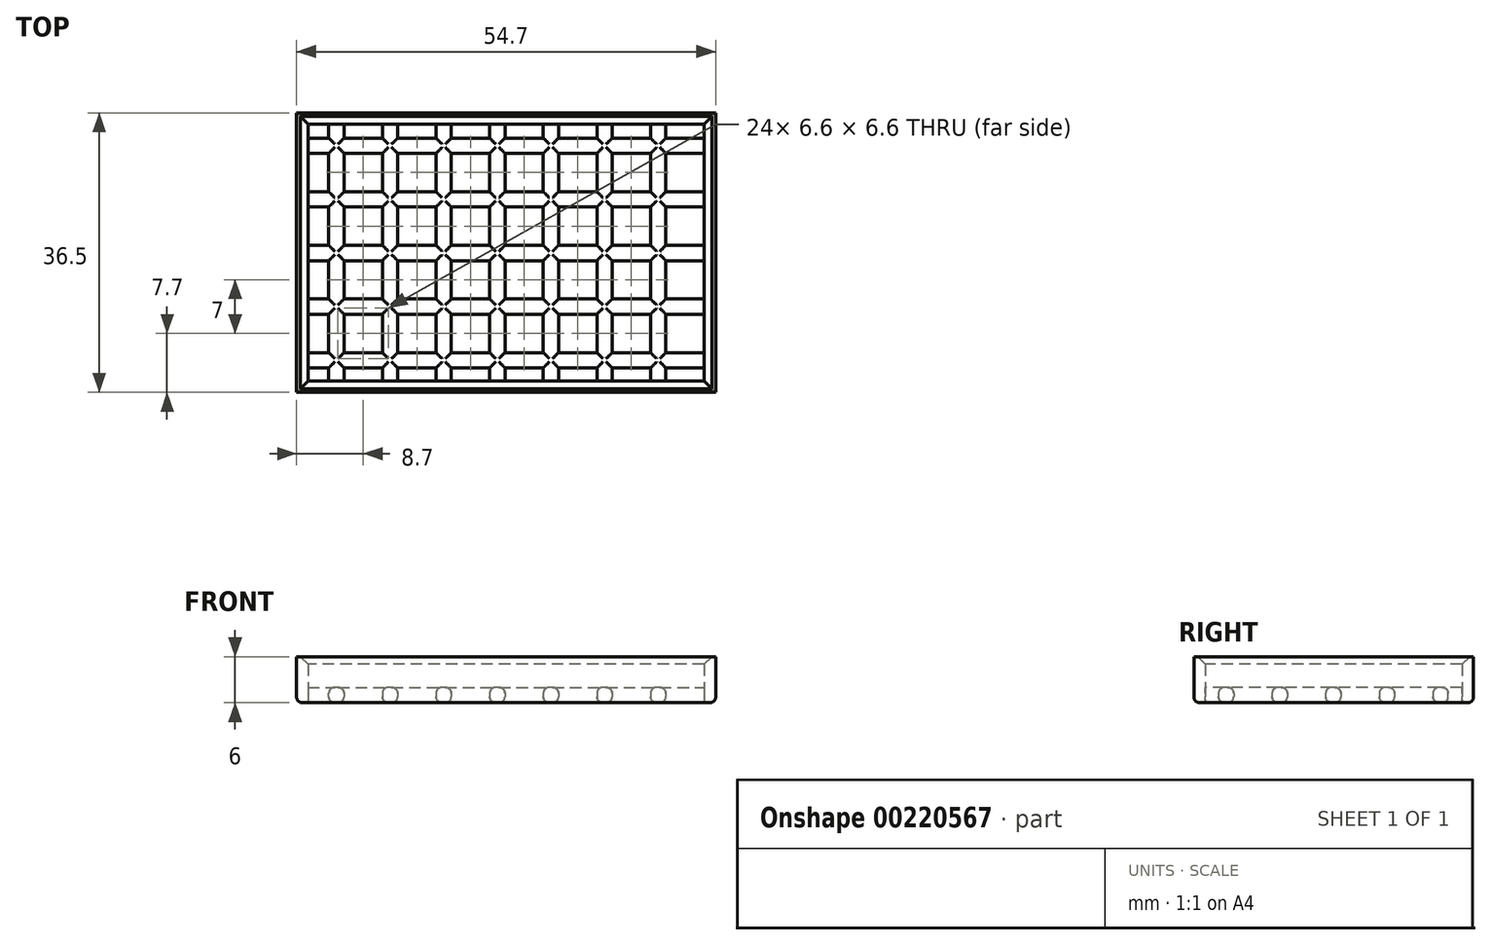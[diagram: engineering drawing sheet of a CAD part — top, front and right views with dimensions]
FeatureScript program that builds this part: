
annotation { "Feature Type Name" : "Feature", "Feature Type Description" : "" }
export const myFeature = defineFeature(function(context is Context, id is Id, definition is map)
    precondition{}
    {
        {
            var Q0;
            Q0=qCreatedBy(makeId("Top.planeOp"),FACE);
            var sketch = newSketch(context, id + "F0", { "sketchPlane" : qUnion([Q0])});
            skLineSegment(sketch, "E0.bottom", {"start": v(0, 36.5) * mm, "end": v(54.7, 36.5) * mm});
            skLineSegment(sketch, "E0.top", {"start": v(0, 0) * mm, "end": v(54.7, 0) * mm});
            skLineSegment(sketch, "E0.left", {"start": v(0, 36.5) * mm, "end": v(0, 0) * mm});
            skLineSegment(sketch, "E0.right", {"start": v(54.7, 36.5) * mm, "end": v(54.7, 0) * mm});
            skSolve(sketch);
        }
        {
            var Q0;
            Q0 = qSketchRegion(id + "F0", true);
            extrude(context, id + "F1", {"entities" : qUnion([Q0]), "oppositeDirection" : true, "depth" : 2 * mm});
        }
        {
            var Q0;
            Q0=makeQuery(id+"F1.opExtrude","CAP_FACE",FACE,{"disambiguationData":[OSD([sQuery(id+"F0.wireOp",EDGE,"E0.bottom"),sQuery(id+"F0.wireOp",EDGE,"E0.top"),sQuery(id+"F0.wireOp",EDGE,"E0.left"),sQuery(id+"F0.wireOp",EDGE,"E0.right")])],"isStart":true});
            var sketch = newSketch(context, id + "F2", { "sketchPlane" : qUnion([Q0])});
            skLineSegment(sketch, "E1.bottom", {"start": v(-0.8, 38.2) * mm, "end": v(4.2, 38.2) * mm});
            skLineSegment(sketch, "E1.top", {"start": v(-0.8, 33.2) * mm, "end": v(4.2, 33.2) * mm});
            skLineSegment(sketch, "E1.left", {"start": v(-0.8, 38.2) * mm, "end": v(-0.8, 33.2) * mm});
            skLineSegment(sketch, "E1.right", {"start": v(4.2, 38.2) * mm, "end": v(4.2, 33.2) * mm});
            skLineSegment(sketch, "E2.0.1.0", {"start": v(-0.8, 31.2) * mm, "end": v(4.2, 31.2) * mm});
            skLineSegment(sketch, "E2.0.1.1", {"start": v(-0.8, 26.2) * mm, "end": v(4.2, 26.2) * mm});
            skLineSegment(sketch, "E2.0.1.2", {"start": v(-0.8, 31.2) * mm, "end": v(-0.8, 26.2) * mm});
            skLineSegment(sketch, "E2.0.1.3", {"start": v(4.2, 31.2) * mm, "end": v(4.2, 26.2) * mm});
            skLineSegment(sketch, "E2.0.2.0", {"start": v(-0.8, 24.2) * mm, "end": v(4.2, 24.2) * mm});
            skLineSegment(sketch, "E2.0.2.1", {"start": v(-0.8, 19.2) * mm, "end": v(4.2, 19.2) * mm});
            skLineSegment(sketch, "E2.0.2.2", {"start": v(-0.8, 24.2) * mm, "end": v(-0.8, 19.2) * mm});
            skLineSegment(sketch, "E2.0.2.3", {"start": v(4.2, 24.2) * mm, "end": v(4.2, 19.2) * mm});
            skLineSegment(sketch, "E2.0.3.0", {"start": v(-0.8, 17.2) * mm, "end": v(4.2, 17.2) * mm});
            skLineSegment(sketch, "E2.0.3.1", {"start": v(-0.8, 12.2) * mm, "end": v(4.2, 12.2) * mm});
            skLineSegment(sketch, "E2.0.3.2", {"start": v(-0.8, 17.2) * mm, "end": v(-0.8, 12.2) * mm});
            skLineSegment(sketch, "E2.0.3.3", {"start": v(4.2, 17.2) * mm, "end": v(4.2, 12.2) * mm});
            skLineSegment(sketch, "E2.0.4.0", {"start": v(-0.8, 10.2) * mm, "end": v(4.2, 10.2) * mm});
            skLineSegment(sketch, "E2.0.4.1", {"start": v(-0.8, 5.2) * mm, "end": v(4.2, 5.2) * mm});
            skLineSegment(sketch, "E2.0.4.2", {"start": v(-0.8, 10.2) * mm, "end": v(-0.8, 5.2) * mm});
            skLineSegment(sketch, "E2.0.4.3", {"start": v(4.2, 10.2) * mm, "end": v(4.2, 5.2) * mm});
            skLineSegment(sketch, "E2.0.5.0", {"start": v(-0.8, 3.2) * mm, "end": v(4.2, 3.2) * mm});
            skLineSegment(sketch, "E2.0.5.1", {"start": v(-0.8, -1.8) * mm, "end": v(4.2, -1.8) * mm});
            skLineSegment(sketch, "E2.0.5.2", {"start": v(-0.8, 3.2) * mm, "end": v(-0.8, -1.8) * mm});
            skLineSegment(sketch, "E2.0.5.3", {"start": v(4.2, 3.2) * mm, "end": v(4.2, -1.8) * mm});
            skLineSegment(sketch, "E2.1.0.0", {"start": v(6.2, 38.2) * mm, "end": v(11.2, 38.2) * mm});
            skLineSegment(sketch, "E2.1.0.1", {"start": v(6.2, 33.2) * mm, "end": v(11.2, 33.2) * mm});
            skLineSegment(sketch, "E2.1.0.2", {"start": v(6.2, 38.2) * mm, "end": v(6.2, 33.2) * mm});
            skLineSegment(sketch, "E2.1.0.3", {"start": v(11.2, 38.2) * mm, "end": v(11.2, 33.2) * mm});
            skLineSegment(sketch, "E2.1.1.0", {"start": v(6.2, 31.2) * mm, "end": v(11.2, 31.2) * mm});
            skLineSegment(sketch, "E2.1.1.1", {"start": v(6.2, 26.2) * mm, "end": v(11.2, 26.2) * mm});
            skLineSegment(sketch, "E2.1.1.2", {"start": v(6.2, 31.2) * mm, "end": v(6.2, 26.2) * mm});
            skLineSegment(sketch, "E2.1.1.3", {"start": v(11.2, 31.2) * mm, "end": v(11.2, 26.2) * mm});
            skLineSegment(sketch, "E2.1.2.0", {"start": v(6.2, 24.2) * mm, "end": v(11.2, 24.2) * mm});
            skLineSegment(sketch, "E2.1.2.1", {"start": v(6.2, 19.2) * mm, "end": v(11.2, 19.2) * mm});
            skLineSegment(sketch, "E2.1.2.2", {"start": v(6.2, 24.2) * mm, "end": v(6.2, 19.2) * mm});
            skLineSegment(sketch, "E2.1.2.3", {"start": v(11.2, 24.2) * mm, "end": v(11.2, 19.2) * mm});
            skLineSegment(sketch, "E2.1.3.0", {"start": v(6.2, 17.2) * mm, "end": v(11.2, 17.2) * mm});
            skLineSegment(sketch, "E2.1.3.1", {"start": v(6.2, 12.2) * mm, "end": v(11.2, 12.2) * mm});
            skLineSegment(sketch, "E2.1.3.2", {"start": v(6.2, 17.2) * mm, "end": v(6.2, 12.2) * mm});
            skLineSegment(sketch, "E2.1.3.3", {"start": v(11.2, 17.2) * mm, "end": v(11.2, 12.2) * mm});
            skLineSegment(sketch, "E2.1.4.0", {"start": v(6.2, 10.2) * mm, "end": v(11.2, 10.2) * mm});
            skLineSegment(sketch, "E2.1.4.1", {"start": v(6.2, 5.2) * mm, "end": v(11.2, 5.2) * mm});
            skLineSegment(sketch, "E2.1.4.2", {"start": v(6.2, 10.2) * mm, "end": v(6.2, 5.2) * mm});
            skLineSegment(sketch, "E2.1.4.3", {"start": v(11.2, 10.2) * mm, "end": v(11.2, 5.2) * mm});
            skLineSegment(sketch, "E2.1.5.0", {"start": v(6.2, 3.2) * mm, "end": v(11.2, 3.2) * mm});
            skLineSegment(sketch, "E2.1.5.1", {"start": v(6.2, -1.8) * mm, "end": v(11.2, -1.8) * mm});
            skLineSegment(sketch, "E2.1.5.2", {"start": v(6.2, 3.2) * mm, "end": v(6.2, -1.8) * mm});
            skLineSegment(sketch, "E2.1.5.3", {"start": v(11.2, 3.2) * mm, "end": v(11.2, -1.8) * mm});
            skLineSegment(sketch, "E2.2.0.0", {"start": v(13.2, 38.2) * mm, "end": v(18.2, 38.2) * mm});
            skLineSegment(sketch, "E2.2.0.1", {"start": v(13.2, 33.2) * mm, "end": v(18.2, 33.2) * mm});
            skLineSegment(sketch, "E2.2.0.2", {"start": v(13.2, 38.2) * mm, "end": v(13.2, 33.2) * mm});
            skLineSegment(sketch, "E2.2.0.3", {"start": v(18.2, 38.2) * mm, "end": v(18.2, 33.2) * mm});
            skLineSegment(sketch, "E2.2.1.0", {"start": v(13.2, 31.2) * mm, "end": v(18.2, 31.2) * mm});
            skLineSegment(sketch, "E2.2.1.1", {"start": v(13.2, 26.2) * mm, "end": v(18.2, 26.2) * mm});
            skLineSegment(sketch, "E2.2.1.2", {"start": v(13.2, 31.2) * mm, "end": v(13.2, 26.2) * mm});
            skLineSegment(sketch, "E2.2.1.3", {"start": v(18.2, 31.2) * mm, "end": v(18.2, 26.2) * mm});
            skLineSegment(sketch, "E2.2.2.0", {"start": v(13.2, 24.2) * mm, "end": v(18.2, 24.2) * mm});
            skLineSegment(sketch, "E2.2.2.1", {"start": v(13.2, 19.2) * mm, "end": v(18.2, 19.2) * mm});
            skLineSegment(sketch, "E2.2.2.2", {"start": v(13.2, 24.2) * mm, "end": v(13.2, 19.2) * mm});
            skLineSegment(sketch, "E2.2.2.3", {"start": v(18.2, 24.2) * mm, "end": v(18.2, 19.2) * mm});
            skLineSegment(sketch, "E2.2.3.0", {"start": v(13.2, 17.2) * mm, "end": v(18.2, 17.2) * mm});
            skLineSegment(sketch, "E2.2.3.1", {"start": v(13.2, 12.2) * mm, "end": v(18.2, 12.2) * mm});
            skLineSegment(sketch, "E2.2.3.2", {"start": v(13.2, 17.2) * mm, "end": v(13.2, 12.2) * mm});
            skLineSegment(sketch, "E2.2.3.3", {"start": v(18.2, 17.2) * mm, "end": v(18.2, 12.2) * mm});
            skLineSegment(sketch, "E2.2.4.0", {"start": v(13.2, 10.2) * mm, "end": v(18.2, 10.2) * mm});
            skLineSegment(sketch, "E2.2.4.1", {"start": v(13.2, 5.2) * mm, "end": v(18.2, 5.2) * mm});
            skLineSegment(sketch, "E2.2.4.2", {"start": v(13.2, 10.2) * mm, "end": v(13.2, 5.2) * mm});
            skLineSegment(sketch, "E2.2.4.3", {"start": v(18.2, 10.2) * mm, "end": v(18.2, 5.2) * mm});
            skLineSegment(sketch, "E2.2.5.0", {"start": v(13.2, 3.2) * mm, "end": v(18.2, 3.2) * mm});
            skLineSegment(sketch, "E2.2.5.1", {"start": v(13.2, -1.8) * mm, "end": v(18.2, -1.8) * mm});
            skLineSegment(sketch, "E2.2.5.2", {"start": v(13.2, 3.2) * mm, "end": v(13.2, -1.8) * mm});
            skLineSegment(sketch, "E2.2.5.3", {"start": v(18.2, 3.2) * mm, "end": v(18.2, -1.8) * mm});
            skLineSegment(sketch, "E2.3.0.0", {"start": v(20.2, 38.2) * mm, "end": v(25.2, 38.2) * mm});
            skLineSegment(sketch, "E2.3.0.1", {"start": v(20.2, 33.2) * mm, "end": v(25.2, 33.2) * mm});
            skLineSegment(sketch, "E2.3.0.2", {"start": v(20.2, 38.2) * mm, "end": v(20.2, 33.2) * mm});
            skLineSegment(sketch, "E2.3.0.3", {"start": v(25.2, 38.2) * mm, "end": v(25.2, 33.2) * mm});
            skLineSegment(sketch, "E2.3.1.0", {"start": v(20.2, 31.2) * mm, "end": v(25.2, 31.2) * mm});
            skLineSegment(sketch, "E2.3.1.1", {"start": v(20.2, 26.2) * mm, "end": v(25.2, 26.2) * mm});
            skLineSegment(sketch, "E2.3.1.2", {"start": v(20.2, 31.2) * mm, "end": v(20.2, 26.2) * mm});
            skLineSegment(sketch, "E2.3.1.3", {"start": v(25.2, 31.2) * mm, "end": v(25.2, 26.2) * mm});
            skLineSegment(sketch, "E2.3.2.0", {"start": v(20.2, 24.2) * mm, "end": v(25.2, 24.2) * mm});
            skLineSegment(sketch, "E2.3.2.1", {"start": v(20.2, 19.2) * mm, "end": v(25.2, 19.2) * mm});
            skLineSegment(sketch, "E2.3.2.2", {"start": v(20.2, 24.2) * mm, "end": v(20.2, 19.2) * mm});
            skLineSegment(sketch, "E2.3.2.3", {"start": v(25.2, 24.2) * mm, "end": v(25.2, 19.2) * mm});
            skLineSegment(sketch, "E2.3.3.0", {"start": v(20.2, 17.2) * mm, "end": v(25.2, 17.2) * mm});
            skLineSegment(sketch, "E2.3.3.1", {"start": v(20.2, 12.2) * mm, "end": v(25.2, 12.2) * mm});
            skLineSegment(sketch, "E2.3.3.2", {"start": v(20.2, 17.2) * mm, "end": v(20.2, 12.2) * mm});
            skLineSegment(sketch, "E2.3.3.3", {"start": v(25.2, 17.2) * mm, "end": v(25.2, 12.2) * mm});
            skLineSegment(sketch, "E2.3.4.0", {"start": v(20.2, 10.2) * mm, "end": v(25.2, 10.2) * mm});
            skLineSegment(sketch, "E2.3.4.1", {"start": v(20.2, 5.2) * mm, "end": v(25.2, 5.2) * mm});
            skLineSegment(sketch, "E2.3.4.2", {"start": v(20.2, 10.2) * mm, "end": v(20.2, 5.2) * mm});
            skLineSegment(sketch, "E2.3.4.3", {"start": v(25.2, 10.2) * mm, "end": v(25.2, 5.2) * mm});
            skLineSegment(sketch, "E2.3.5.0", {"start": v(20.2, 3.2) * mm, "end": v(25.2, 3.2) * mm});
            skLineSegment(sketch, "E2.3.5.1", {"start": v(20.2, -1.8) * mm, "end": v(25.2, -1.8) * mm});
            skLineSegment(sketch, "E2.3.5.2", {"start": v(20.2, 3.2) * mm, "end": v(20.2, -1.8) * mm});
            skLineSegment(sketch, "E2.3.5.3", {"start": v(25.2, 3.2) * mm, "end": v(25.2, -1.8) * mm});
            skLineSegment(sketch, "E2.4.0.0", {"start": v(27.2, 38.2) * mm, "end": v(32.2, 38.2) * mm});
            skLineSegment(sketch, "E2.4.0.1", {"start": v(27.2, 33.2) * mm, "end": v(32.2, 33.2) * mm});
            skLineSegment(sketch, "E2.4.0.2", {"start": v(27.2, 38.2) * mm, "end": v(27.2, 33.2) * mm});
            skLineSegment(sketch, "E2.4.0.3", {"start": v(32.2, 38.2) * mm, "end": v(32.2, 33.2) * mm});
            skLineSegment(sketch, "E2.4.1.0", {"start": v(27.2, 31.2) * mm, "end": v(32.2, 31.2) * mm});
            skLineSegment(sketch, "E2.4.1.1", {"start": v(27.2, 26.2) * mm, "end": v(32.2, 26.2) * mm});
            skLineSegment(sketch, "E2.4.1.2", {"start": v(27.2, 31.2) * mm, "end": v(27.2, 26.2) * mm});
            skLineSegment(sketch, "E2.4.1.3", {"start": v(32.2, 31.2) * mm, "end": v(32.2, 26.2) * mm});
            skLineSegment(sketch, "E2.4.2.0", {"start": v(27.2, 24.2) * mm, "end": v(32.2, 24.2) * mm});
            skLineSegment(sketch, "E2.4.2.1", {"start": v(27.2, 19.2) * mm, "end": v(32.2, 19.2) * mm});
            skLineSegment(sketch, "E2.4.2.2", {"start": v(27.2, 24.2) * mm, "end": v(27.2, 19.2) * mm});
            skLineSegment(sketch, "E2.4.2.3", {"start": v(32.2, 24.2) * mm, "end": v(32.2, 19.2) * mm});
            skLineSegment(sketch, "E2.4.3.0", {"start": v(27.2, 17.2) * mm, "end": v(32.2, 17.2) * mm});
            skLineSegment(sketch, "E2.4.3.1", {"start": v(27.2, 12.2) * mm, "end": v(32.2, 12.2) * mm});
            skLineSegment(sketch, "E2.4.3.2", {"start": v(27.2, 17.2) * mm, "end": v(27.2, 12.2) * mm});
            skLineSegment(sketch, "E2.4.3.3", {"start": v(32.2, 17.2) * mm, "end": v(32.2, 12.2) * mm});
            skLineSegment(sketch, "E2.4.4.0", {"start": v(27.2, 10.2) * mm, "end": v(32.2, 10.2) * mm});
            skLineSegment(sketch, "E2.4.4.1", {"start": v(27.2, 5.2) * mm, "end": v(32.2, 5.2) * mm});
            skLineSegment(sketch, "E2.4.4.2", {"start": v(27.2, 10.2) * mm, "end": v(27.2, 5.2) * mm});
            skLineSegment(sketch, "E2.4.4.3", {"start": v(32.2, 10.2) * mm, "end": v(32.2, 5.2) * mm});
            skLineSegment(sketch, "E2.4.5.0", {"start": v(27.2, 3.2) * mm, "end": v(32.2, 3.2) * mm});
            skLineSegment(sketch, "E2.4.5.1", {"start": v(27.2, -1.8) * mm, "end": v(32.2, -1.8) * mm});
            skLineSegment(sketch, "E2.4.5.2", {"start": v(27.2, 3.2) * mm, "end": v(27.2, -1.8) * mm});
            skLineSegment(sketch, "E2.4.5.3", {"start": v(32.2, 3.2) * mm, "end": v(32.2, -1.8) * mm});
            skLineSegment(sketch, "E2.5.0.0", {"start": v(34.2, 38.2) * mm, "end": v(39.2, 38.2) * mm});
            skLineSegment(sketch, "E2.5.0.1", {"start": v(34.2, 33.2) * mm, "end": v(39.2, 33.2) * mm});
            skLineSegment(sketch, "E2.5.0.2", {"start": v(34.2, 38.2) * mm, "end": v(34.2, 33.2) * mm});
            skLineSegment(sketch, "E2.5.0.3", {"start": v(39.2, 38.2) * mm, "end": v(39.2, 33.2) * mm});
            skLineSegment(sketch, "E2.5.1.0", {"start": v(34.2, 31.2) * mm, "end": v(39.2, 31.2) * mm});
            skLineSegment(sketch, "E2.5.1.1", {"start": v(34.2, 26.2) * mm, "end": v(39.2, 26.2) * mm});
            skLineSegment(sketch, "E2.5.1.2", {"start": v(34.2, 31.2) * mm, "end": v(34.2, 26.2) * mm});
            skLineSegment(sketch, "E2.5.1.3", {"start": v(39.2, 31.2) * mm, "end": v(39.2, 26.2) * mm});
            skLineSegment(sketch, "E2.5.2.0", {"start": v(34.2, 24.2) * mm, "end": v(39.2, 24.2) * mm});
            skLineSegment(sketch, "E2.5.2.1", {"start": v(34.2, 19.2) * mm, "end": v(39.2, 19.2) * mm});
            skLineSegment(sketch, "E2.5.2.2", {"start": v(34.2, 24.2) * mm, "end": v(34.2, 19.2) * mm});
            skLineSegment(sketch, "E2.5.2.3", {"start": v(39.2, 24.2) * mm, "end": v(39.2, 19.2) * mm});
            skLineSegment(sketch, "E2.5.3.0", {"start": v(34.2, 17.2) * mm, "end": v(39.2, 17.2) * mm});
            skLineSegment(sketch, "E2.5.3.1", {"start": v(34.2, 12.2) * mm, "end": v(39.2, 12.2) * mm});
            skLineSegment(sketch, "E2.5.3.2", {"start": v(34.2, 17.2) * mm, "end": v(34.2, 12.2) * mm});
            skLineSegment(sketch, "E2.5.3.3", {"start": v(39.2, 17.2) * mm, "end": v(39.2, 12.2) * mm});
            skLineSegment(sketch, "E2.5.4.0", {"start": v(34.2, 10.2) * mm, "end": v(39.2, 10.2) * mm});
            skLineSegment(sketch, "E2.5.4.1", {"start": v(34.2, 5.2) * mm, "end": v(39.2, 5.2) * mm});
            skLineSegment(sketch, "E2.5.4.2", {"start": v(34.2, 10.2) * mm, "end": v(34.2, 5.2) * mm});
            skLineSegment(sketch, "E2.5.4.3", {"start": v(39.2, 10.2) * mm, "end": v(39.2, 5.2) * mm});
            skLineSegment(sketch, "E2.5.5.0", {"start": v(34.2, 3.2) * mm, "end": v(39.2, 3.2) * mm});
            skLineSegment(sketch, "E2.5.5.1", {"start": v(34.2, -1.8) * mm, "end": v(39.2, -1.8) * mm});
            skLineSegment(sketch, "E2.5.5.2", {"start": v(34.2, 3.2) * mm, "end": v(34.2, -1.8) * mm});
            skLineSegment(sketch, "E2.5.5.3", {"start": v(39.2, 3.2) * mm, "end": v(39.2, -1.8) * mm});
            skLineSegment(sketch, "E2.6.0.0", {"start": v(41.2, 38.2) * mm, "end": v(46.2, 38.2) * mm});
            skLineSegment(sketch, "E2.6.0.1", {"start": v(41.2, 33.2) * mm, "end": v(46.2, 33.2) * mm});
            skLineSegment(sketch, "E2.6.0.2", {"start": v(41.2, 38.2) * mm, "end": v(41.2, 33.2) * mm});
            skLineSegment(sketch, "E2.6.0.3", {"start": v(46.2, 38.2) * mm, "end": v(46.2, 33.2) * mm});
            skLineSegment(sketch, "E2.6.1.0", {"start": v(41.2, 31.2) * mm, "end": v(46.2, 31.2) * mm});
            skLineSegment(sketch, "E2.6.1.1", {"start": v(41.2, 26.2) * mm, "end": v(46.2, 26.2) * mm});
            skLineSegment(sketch, "E2.6.1.2", {"start": v(41.2, 31.2) * mm, "end": v(41.2, 26.2) * mm});
            skLineSegment(sketch, "E2.6.1.3", {"start": v(46.2, 31.2) * mm, "end": v(46.2, 26.2) * mm});
            skLineSegment(sketch, "E2.6.2.0", {"start": v(41.2, 24.2) * mm, "end": v(46.2, 24.2) * mm});
            skLineSegment(sketch, "E2.6.2.1", {"start": v(41.2, 19.2) * mm, "end": v(46.2, 19.2) * mm});
            skLineSegment(sketch, "E2.6.2.2", {"start": v(41.2, 24.2) * mm, "end": v(41.2, 19.2) * mm});
            skLineSegment(sketch, "E2.6.2.3", {"start": v(46.2, 24.2) * mm, "end": v(46.2, 19.2) * mm});
            skLineSegment(sketch, "E2.6.3.0", {"start": v(41.2, 17.2) * mm, "end": v(46.2, 17.2) * mm});
            skLineSegment(sketch, "E2.6.3.1", {"start": v(41.2, 12.2) * mm, "end": v(46.2, 12.2) * mm});
            skLineSegment(sketch, "E2.6.3.2", {"start": v(41.2, 17.2) * mm, "end": v(41.2, 12.2) * mm});
            skLineSegment(sketch, "E2.6.3.3", {"start": v(46.2, 17.2) * mm, "end": v(46.2, 12.2) * mm});
            skLineSegment(sketch, "E2.6.4.0", {"start": v(41.2, 10.2) * mm, "end": v(46.2, 10.2) * mm});
            skLineSegment(sketch, "E2.6.4.1", {"start": v(41.2, 5.2) * mm, "end": v(46.2, 5.2) * mm});
            skLineSegment(sketch, "E2.6.4.2", {"start": v(41.2, 10.2) * mm, "end": v(41.2, 5.2) * mm});
            skLineSegment(sketch, "E2.6.4.3", {"start": v(46.2, 10.2) * mm, "end": v(46.2, 5.2) * mm});
            skLineSegment(sketch, "E2.6.5.0", {"start": v(41.2, 3.2) * mm, "end": v(46.2, 3.2) * mm});
            skLineSegment(sketch, "E2.6.5.1", {"start": v(41.2, -1.8) * mm, "end": v(46.2, -1.8) * mm});
            skLineSegment(sketch, "E2.6.5.2", {"start": v(41.2, 3.2) * mm, "end": v(41.2, -1.8) * mm});
            skLineSegment(sketch, "E2.6.5.3", {"start": v(46.2, 3.2) * mm, "end": v(46.2, -1.8) * mm});
            skLineSegment(sketch, "E2.7.0.0", {"start": v(48.2, 38.2) * mm, "end": v(53.2, 38.2) * mm});
            skLineSegment(sketch, "E2.7.0.1", {"start": v(48.2, 33.2) * mm, "end": v(53.2, 33.2) * mm});
            skLineSegment(sketch, "E2.7.0.2", {"start": v(48.2, 38.2) * mm, "end": v(48.2, 33.2) * mm});
            skLineSegment(sketch, "E2.7.0.3", {"start": v(53.2, 38.2) * mm, "end": v(53.2, 33.2) * mm});
            skLineSegment(sketch, "E2.7.1.0", {"start": v(48.2, 31.2) * mm, "end": v(53.2, 31.2) * mm});
            skLineSegment(sketch, "E2.7.1.1", {"start": v(48.2, 26.2) * mm, "end": v(53.2, 26.2) * mm});
            skLineSegment(sketch, "E2.7.1.2", {"start": v(48.2, 31.2) * mm, "end": v(48.2, 26.2) * mm});
            skLineSegment(sketch, "E2.7.1.3", {"start": v(53.2, 31.2) * mm, "end": v(53.2, 26.2) * mm});
            skLineSegment(sketch, "E2.7.2.0", {"start": v(48.2, 24.2) * mm, "end": v(53.2, 24.2) * mm});
            skLineSegment(sketch, "E2.7.2.1", {"start": v(48.2, 19.2) * mm, "end": v(53.2, 19.2) * mm});
            skLineSegment(sketch, "E2.7.2.2", {"start": v(48.2, 24.2) * mm, "end": v(48.2, 19.2) * mm});
            skLineSegment(sketch, "E2.7.2.3", {"start": v(53.2, 24.2) * mm, "end": v(53.2, 19.2) * mm});
            skLineSegment(sketch, "E2.7.3.0", {"start": v(48.2, 17.2) * mm, "end": v(53.2, 17.2) * mm});
            skLineSegment(sketch, "E2.7.3.1", {"start": v(48.2, 12.2) * mm, "end": v(53.2, 12.2) * mm});
            skLineSegment(sketch, "E2.7.3.2", {"start": v(48.2, 17.2) * mm, "end": v(48.2, 12.2) * mm});
            skLineSegment(sketch, "E2.7.3.3", {"start": v(53.2, 17.2) * mm, "end": v(53.2, 12.2) * mm});
            skLineSegment(sketch, "E2.7.4.0", {"start": v(48.2, 10.2) * mm, "end": v(53.2, 10.2) * mm});
            skLineSegment(sketch, "E2.7.4.1", {"start": v(48.2, 5.2) * mm, "end": v(53.2, 5.2) * mm});
            skLineSegment(sketch, "E2.7.4.2", {"start": v(48.2, 10.2) * mm, "end": v(48.2, 5.2) * mm});
            skLineSegment(sketch, "E2.7.4.3", {"start": v(53.2, 10.2) * mm, "end": v(53.2, 5.2) * mm});
            skLineSegment(sketch, "E2.7.5.0", {"start": v(48.2, 3.2) * mm, "end": v(53.2, 3.2) * mm});
            skLineSegment(sketch, "E2.7.5.1", {"start": v(48.2, -1.8) * mm, "end": v(53.2, -1.8) * mm});
            skLineSegment(sketch, "E2.7.5.2", {"start": v(48.2, 3.2) * mm, "end": v(48.2, -1.8) * mm});
            skLineSegment(sketch, "E2.7.5.3", {"start": v(53.2, 3.2) * mm, "end": v(53.2, -1.8) * mm});
            skLineSegment(sketch, "E2.direction1", {"start": v(-0.8, 33.2) * mm, "end": v(6.2, 33.2) * mm, "construction": true});
            skLineSegment(sketch, "E2.direction2", {"start": v(-0.8, 33.2) * mm, "end": v(-0.8, 26.2) * mm, "construction": true});
            skLineSegment(sketch, "E3.bottom", {"start": v(53.2, 38.2) * mm, "end": v(57.35, 38.2) * mm});
            skLineSegment(sketch, "E3.top", {"start": v(53.2, 33.2) * mm, "end": v(57.35, 33.2) * mm});
            skLineSegment(sketch, "E3.right", {"start": v(57.35, 38.2) * mm, "end": v(57.35, 33.2) * mm});
            skLineSegment(sketch, "E4.1.0.0", {"start": v(53.2, 26.2) * mm, "end": v(57.35, 26.2) * mm});
            skLineSegment(sketch, "E4.1.0.1", {"start": v(57.35, 31.2) * mm, "end": v(57.35, 26.2) * mm});
            skLineSegment(sketch, "E4.1.0.2", {"start": v(53.2, 31.2) * mm, "end": v(57.35, 31.2) * mm});
            skLineSegment(sketch, "E4.2.0.0", {"start": v(53.2, 19.2) * mm, "end": v(57.35, 19.2) * mm});
            skLineSegment(sketch, "E4.2.0.1", {"start": v(57.35, 24.2) * mm, "end": v(57.35, 19.2) * mm});
            skLineSegment(sketch, "E4.2.0.2", {"start": v(53.2, 24.2) * mm, "end": v(57.35, 24.2) * mm});
            skLineSegment(sketch, "E4.3.0.0", {"start": v(53.2, 12.2) * mm, "end": v(57.35, 12.2) * mm});
            skLineSegment(sketch, "E4.3.0.1", {"start": v(57.35, 17.2) * mm, "end": v(57.35, 12.2) * mm});
            skLineSegment(sketch, "E4.3.0.2", {"start": v(53.2, 17.2) * mm, "end": v(57.35, 17.2) * mm});
            skLineSegment(sketch, "E4.4.0.0", {"start": v(53.2, 5.2) * mm, "end": v(57.35, 5.2) * mm});
            skLineSegment(sketch, "E4.4.0.1", {"start": v(57.35, 10.2) * mm, "end": v(57.35, 5.2) * mm});
            skLineSegment(sketch, "E4.4.0.2", {"start": v(53.2, 10.2) * mm, "end": v(57.35, 10.2) * mm});
            skLineSegment(sketch, "E4.5.0.0", {"start": v(53.2, -1.8) * mm, "end": v(57.35, -1.8) * mm});
            skLineSegment(sketch, "E4.5.0.1", {"start": v(57.35, 3.2) * mm, "end": v(57.35, -1.8) * mm});
            skLineSegment(sketch, "E4.5.0.2", {"start": v(53.2, 3.2) * mm, "end": v(57.35, 3.2) * mm});
            skLineSegment(sketch, "E4.direction1", {"start": v(53.2, 33.2) * mm, "end": v(53.2, 26.2) * mm, "construction": true});
            skSolve(sketch);
        }
        {
            var Q0;
            Q0 = qSketchRegion(id + "F2", true);
            extrude(context, id + "F3", {"entities" : qUnion([Q0]), "operationType" : NewBodyOperationType.REMOVE, "endBound" : BoundingType.THROUGH_ALL, "oppositeDirection" : true, "depth" : 25 * mm});
        }
        {
            var Q0;
            Q0=makeQuery(id+"F1.opExtrude","CAP_FACE",FACE,{"disambiguationData":[OSD([sQuery(id+"F0.wireOp",EDGE,"E0.bottom"),sQuery(id+"F0.wireOp",EDGE,"E0.top"),sQuery(id+"F0.wireOp",EDGE,"E0.left"),sQuery(id+"F0.wireOp",EDGE,"E0.right")])],"isStart":false});
            var sketch = newSketch(context, id + "F4", { "sketchPlane" : qUnion([Q0])});
            skLineSegment(sketch, "E5.bottom", {"start": v(0, 0) * mm, "end": v(54.7, 0) * mm});
            skLineSegment(sketch, "E5.top", {"start": v(0, -36.5) * mm, "end": v(54.7, -36.5) * mm});
            skLineSegment(sketch, "E5.left", {"start": v(0, 0) * mm, "end": v(0, -36.5) * mm});
            skLineSegment(sketch, "E5.right", {"start": v(54.7, 0) * mm, "end": v(54.7, -36.5) * mm});
            skLineSegment(sketch, "E6.0", {"start": v(1.5, -1.5) * mm, "end": v(1.5, -35) * mm});
            skLineSegment(sketch, "E6.1", {"start": v(1.5, -1.5) * mm, "end": v(53.2, -1.5) * mm});
            skLineSegment(sketch, "E6.2", {"start": v(53.2, -1.5) * mm, "end": v(53.2, -35) * mm});
            skLineSegment(sketch, "E6.3", {"start": v(1.5, -35) * mm, "end": v(53.2, -35) * mm});
            skSolve(sketch);
        }
        {
            var Q0;
            Q0=makeQuery(id+"F1.opExtrude","CAP_FACE",FACE,{"disambiguationData":[OSD([sQuery(id+"F0.wireOp",EDGE,"E0.bottom"),sQuery(id+"F0.wireOp",EDGE,"E0.top"),sQuery(id+"F0.wireOp",EDGE,"E0.left"),sQuery(id+"F0.wireOp",EDGE,"E0.right")])],"isStart":true});
            var Q1;
            Q1=makeQuery(id+"F1.opExtrude","CAP_FACE",FACE,{"disambiguationData":[OSD([sQuery(id+"F0.wireOp",EDGE,"E0.bottom"),sQuery(id+"F0.wireOp",EDGE,"E0.top"),sQuery(id+"F0.wireOp",EDGE,"E0.left"),sQuery(id+"F0.wireOp",EDGE,"E0.right")])],"isStart":false});
            fillet(context, id + "F5", {"entities" : qUnion([Q0, Q1]), "radius" : 0.8 * mm, "defaultsChanged" : true, "vertexSettings" : [], "allowEdgeOverflow" : false});
        }
        {
            var Q0;
            Q0 = qSketchRegion(id + "F4", true);
            extrude(context, id + "F6", {"entities" : qUnion([Q0]), "operationType" : NewBodyOperationType.ADD, "oppositeDirection" : true, "depth" : 6 * mm});
        }
        {
            var Q0;
            Q0=makeQuery(id+"F6.opExtrude","CAP_EDGE",EDGE,{"disambiguationData":[OSD([sQuery(id+"F4.wireOp",EDGE,"E5.left")])],"isStart":true});
            var Q1;
            Q1=makeQuery(id+"F6.opExtrude","CAP_EDGE",EDGE,{"disambiguationData":[OSD([sQuery(id+"F4.wireOp",EDGE,"E5.bottom")])],"isStart":true});
            var Q2;
            Q2=makeQuery(id+"F6.opExtrude","CAP_EDGE",EDGE,{"disambiguationData":[OSD([sQuery(id+"F4.wireOp",EDGE,"E5.right")])],"isStart":true});
            var Q3;
            Q3=makeQuery(id+"F6.opExtrude","CAP_EDGE",EDGE,{"disambiguationData":[OSD([sQuery(id+"F4.wireOp",EDGE,"E5.top")])],"isStart":true});
            fillet(context, id + "F7", {"entities" : qUnion([Q0, Q1, Q2, Q3]), "radius" : 0.75 * mm, "tangentPropagation" : true, "allowEdgeOverflow" : false});
        }
        {
            var Q0;
            Q0=makeQuery(id+"F6.opExtrude","CAP_EDGE",EDGE,{"disambiguationData":[OSD([sQuery(id+"F4.wireOp",EDGE,"E6.3")])],"isStart":false});
            var Q1;
            Q1=makeQuery(id+"F6.opExtrude","CAP_EDGE",EDGE,{"disambiguationData":[OSD([sQuery(id+"F4.wireOp",EDGE,"E6.0")])],"isStart":false});
            var Q2;
            Q2=makeQuery(id+"F6.opExtrude","CAP_EDGE",EDGE,{"disambiguationData":[OSD([sQuery(id+"F4.wireOp",EDGE,"E6.1")])],"isStart":false});
            var Q3;
            Q3=makeQuery(id+"F6.opExtrude","CAP_EDGE",EDGE,{"disambiguationData":[OSD([sQuery(id+"F4.wireOp",EDGE,"E6.2")])],"isStart":false});
            chamfer(context, id + "F8", {"entities" : qUnion([Q0, Q1, Q2, Q3]), "width" : 1 * mm, "tangentPropagation" : true});
        }
    });
